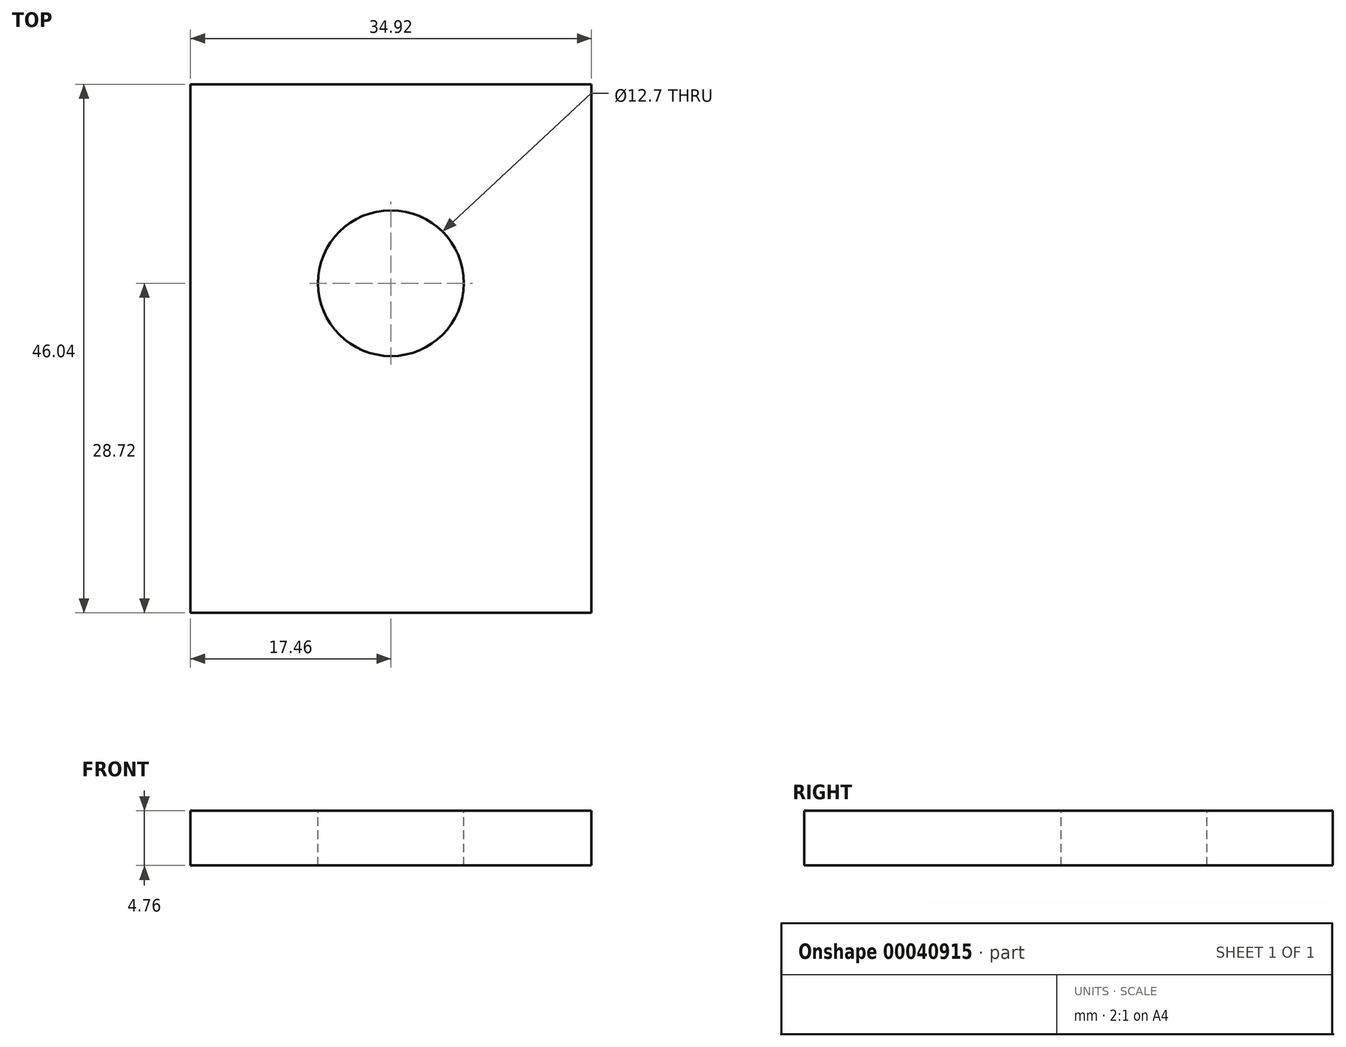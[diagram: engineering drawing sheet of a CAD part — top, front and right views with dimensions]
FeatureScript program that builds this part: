
annotation { "Feature Type Name" : "Feature", "Feature Type Description" : "" }
export const myFeature = defineFeature(function(context is Context, id is Id, definition is map)
    precondition{}
    {
        {
            var Q0;
            Q0=qCreatedBy(makeId("Top.planeOp"),FACE);
            var sketch = newSketch(context, id + "F0", { "sketchPlane" : qUnion([Q0])});
            skLineSegment(sketch, "E0.bottom", {"start": v(-17.46, 0) * mm, "end": v(17.46, 0) * mm});
            skLineSegment(sketch, "E0.top", {"start": v(-17.46, -46.04) * mm, "end": v(17.46, -46.04) * mm});
            skLineSegment(sketch, "E0.left", {"start": v(-17.46, 0) * mm, "end": v(-17.46, -46.04) * mm});
            skLineSegment(sketch, "E0.right", {"start": v(17.46, 0) * mm, "end": v(17.46, -46.04) * mm});
            skPoint(sketch, "E1", {"position": v(0, 0) * mm});
            skSolve(sketch);
        }
        {
            var Q0;
            Q0=makeQuery(id+"F0.imprint","IMPRINT",FACE,{"disambiguationData":[TD([[makeQuery(id+"F0.imprint","IMPRINT",EDGE,{"derivedFrom":sQuery(id+"F0.wireOp",EDGE,"E0.bottom")}),-1.0]])]});
            extrude(context, id + "F1", {"entities" : qUnion([Q0]), "oppositeDirection" : true, "depth" : 4.76 * mm});
        }
        {
            var Q0;
            Q0=makeQuery(id+"F1.opExtrude","CAP_FACE",FACE,{"disambiguationData":[OSD([sQuery(id+"F0.wireOp",EDGE,"E0.bottom"),sQuery(id+"F0.wireOp",EDGE,"E0.top"),sQuery(id+"F0.wireOp",EDGE,"E0.left"),sQuery(id+"F0.wireOp",EDGE,"E0.right")])],"isStart":true});
            var sketch = newSketch(context, id + "F2", { "sketchPlane" : qUnion([Q0])});
            skPoint(sketch, "E2", {"position": v(0, -17.32) * mm});
            skCircle(sketch, "E3.cCircle", {"center": v(0, -17.32) * mm, "radius": 9.5 * mm, "construction": true});
            skLineSegment(sketch, "E3.0", {"start": v(9.5, -22.8) * mm, "end": v(0, -28.29) * mm});
            skLineSegment(sketch, "E3.1", {"start": v(0, -28.29) * mm, "end": v(-9.5, -22.8) * mm});
            skLineSegment(sketch, "E3.2", {"start": v(-9.5, -22.8) * mm, "end": v(-9.5, -11.83) * mm});
            skLineSegment(sketch, "E3.3", {"start": v(-9.5, -11.83) * mm, "end": v(0, -6.35) * mm});
            skLineSegment(sketch, "E3.4", {"start": v(0, -6.35) * mm, "end": v(9.5, -11.83) * mm});
            skLineSegment(sketch, "E3.5", {"start": v(9.5, -11.83) * mm, "end": v(9.5, -22.8) * mm});
            skPoint(sketch, "E3.0.midPoint", {"position": v(4.75, -25.55) * mm});
            skCircle(sketch, "E4", {"center": v(0, -17.32) * mm, "radius": 12 * mm});
            skSolve(sketch);
        }
        {
            var Q0;
            Q0=sQuery(id+"F2.wireOp",VERTEX,"E2");
            var Q1;
            Q1=makeQuery(id+"F1.opExtrude","SWEPT_BODY",BODY,{"disambiguationData":[OSD([sQuery(id+"F0.wireOp",EDGE,"E0.bottom"),sQuery(id+"F0.wireOp",EDGE,"E0.top"),sQuery(id+"F0.wireOp",EDGE,"E0.left"),sQuery(id+"F0.wireOp",EDGE,"E0.right")])]});
            hole(context, id + "F3", {"style" : HoleStyle.SIMPLE, "holeDiameter" : 12.7 * mm, "endStyle" : HoleEndStyle.THROUGH, "locations" : qUnion([Q0]), "scope" : qUnion([Q1])});
        }
    });
